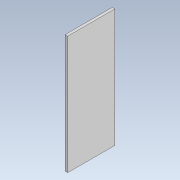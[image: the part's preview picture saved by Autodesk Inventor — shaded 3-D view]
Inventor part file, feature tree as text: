
AUTODESK INVENTOR PART (.ipt)
format: ipt  version: 2021 (Build 250183000, 183)  size: 75,776 bytes
history: native  units: mm
features: other x1, extrude x1, sketch x1
ambient origin geometry x8: Origin, YZ Plane, XZ Plane, XY Plane, X Axis, Y Axis, Z Axis, Center Point
bodies: Body1 (feature_tree)
feature tree (3):
  other  "Sólido1"
  extrude  "Extrusión1"  Depth=45.0mm
  sketch  "Boceto1"  dims[d0=1.0mm d1=0.0mm d2=45.0mm d3=18.0mm]
